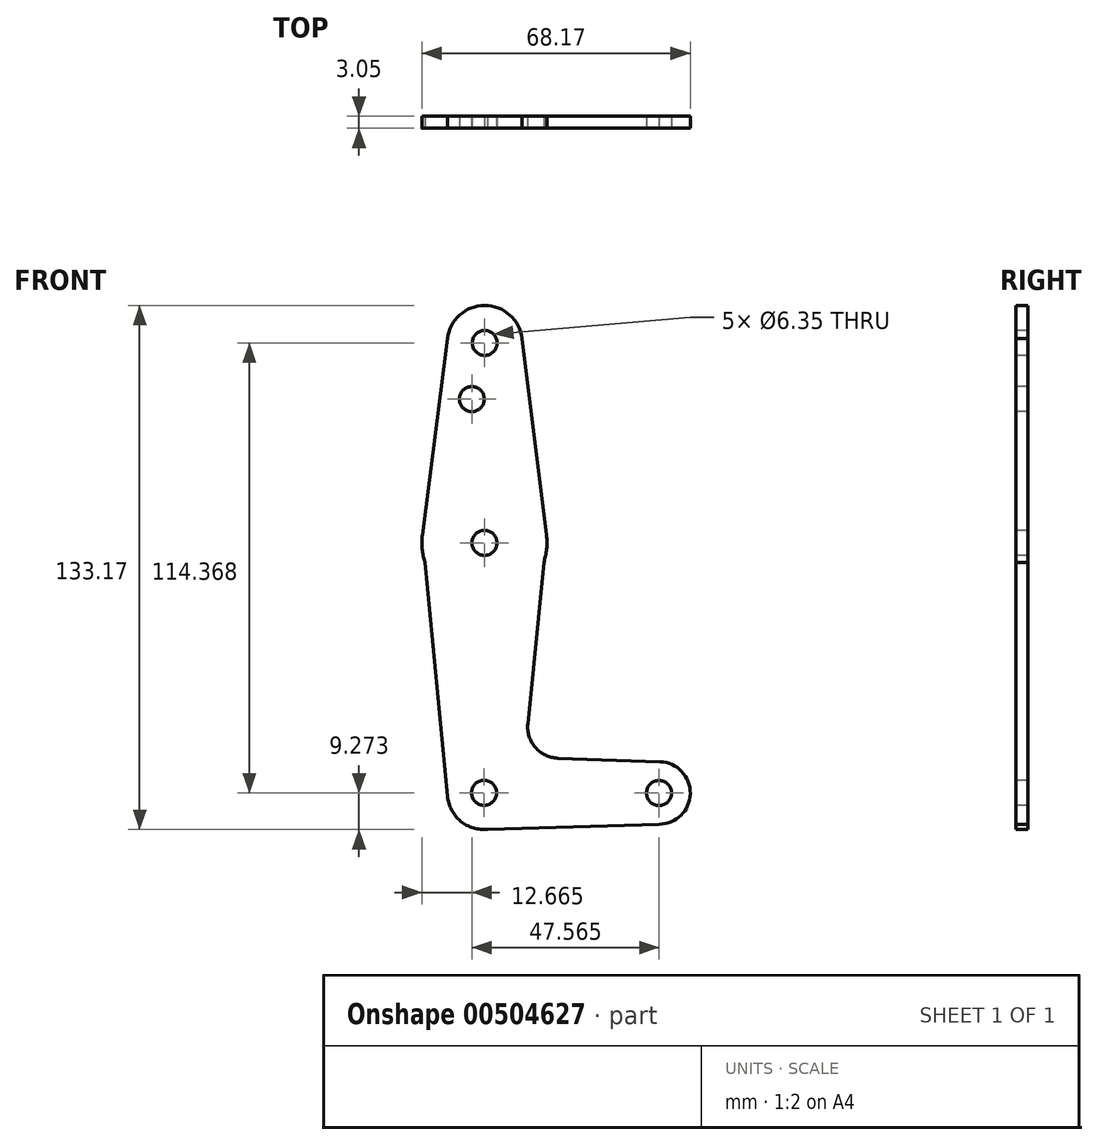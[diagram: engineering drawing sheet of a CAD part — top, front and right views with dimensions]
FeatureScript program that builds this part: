
annotation { "Feature Type Name" : "Feature", "Feature Type Description" : "" }
export const myFeature = defineFeature(function(context is Context, id is Id, definition is map)
    precondition{}
    {
        {
            var Q0;
            Q0=qCreatedBy(makeId("Front.planeOp"),FACE);
            var sketch = newSketch(context, id + "F0", { "sketchPlane" : qUnion([Q0])});
            skPoint(sketch, "E0", {"position": v(0, -74.55) * mm});
            skLineSegment(sketch, "E1", {"start": v(0.18, 39.75) * mm, "end": v(0, -74.55) * mm, "construction": true});
            skLineSegment(sketch, "E2", {"start": v(0, -74.55) * mm, "end": v(44.45, -74.62) * mm, "construction": true});
            skCircle(sketch, "E3", {"center": v(0, -74.55) * mm, "radius": 9.34 * mm});
            skCircle(sketch, "E4", {"center": v(0.1, -11.05) * mm, "radius": 15.88 * mm});
            skCircle(sketch, "E5", {"center": v(0.18, 39.75) * mm, "radius": 9.53 * mm});
            skCircle(sketch, "E6", {"center": v(44.45, -74.62) * mm, "radius": 7.94 * mm});
            skLineSegment(sketch, "E7", {"start": v(-9.3, 40.81) * mm, "end": v(-15.65, -9.04) * mm});
            skLineSegment(sketch, "E8", {"start": v(-15.65, -9.04) * mm, "end": v(-9.3, -75.44) * mm});
            skLineSegment(sketch, "E9", {"start": v(9.64, 40.81) * mm, "end": v(15.85, -9.09) * mm});
            skLineSegment(sketch, "E10", {"start": v(15.85, -9.09) * mm, "end": v(11.12, -57.03) * mm});
            skCircle(sketch, "E11", {"center": v(0.18, 39.75) * mm, "radius": 3.18 * mm});
            skCircle(sketch, "E12", {"center": v(-3.11, 25.48) * mm, "radius": 3.18 * mm});
            skCircle(sketch, "E13", {"center": v(0.1, -11.05) * mm, "radius": 3.18 * mm});
            skLineSegment(sketch, "E14", {"start": v(-0.38, -83.88) * mm, "end": v(44.45, -82.55) * mm});
            skLineSegment(sketch, "E15", {"start": v(44.73, -66.68) * mm, "end": v(18.75, -65.76) * mm});
            skCircle(sketch, "E16", {"center": v(0, -74.55) * mm, "radius": 3.18 * mm});
            skCircle(sketch, "E17", {"center": v(44.45, -74.62) * mm, "radius": 3.18 * mm});
            skArc(sketch, "E18.filletArc", {"start": v(11.12, -57.03) * mm, "mid": v(13.04, -63.05) * mm, "end": v(18.75, -65.76) * mm});
            skSolve(sketch);
        }
        {
            var Q0;
            Q0 = qSketchRegion(id + "F0", true);
            extrude(context, id + "F1", {"entities" : qUnion([Q0]), "oppositeDirection" : true, "depth" : 3.05 * mm});
        }
    });
